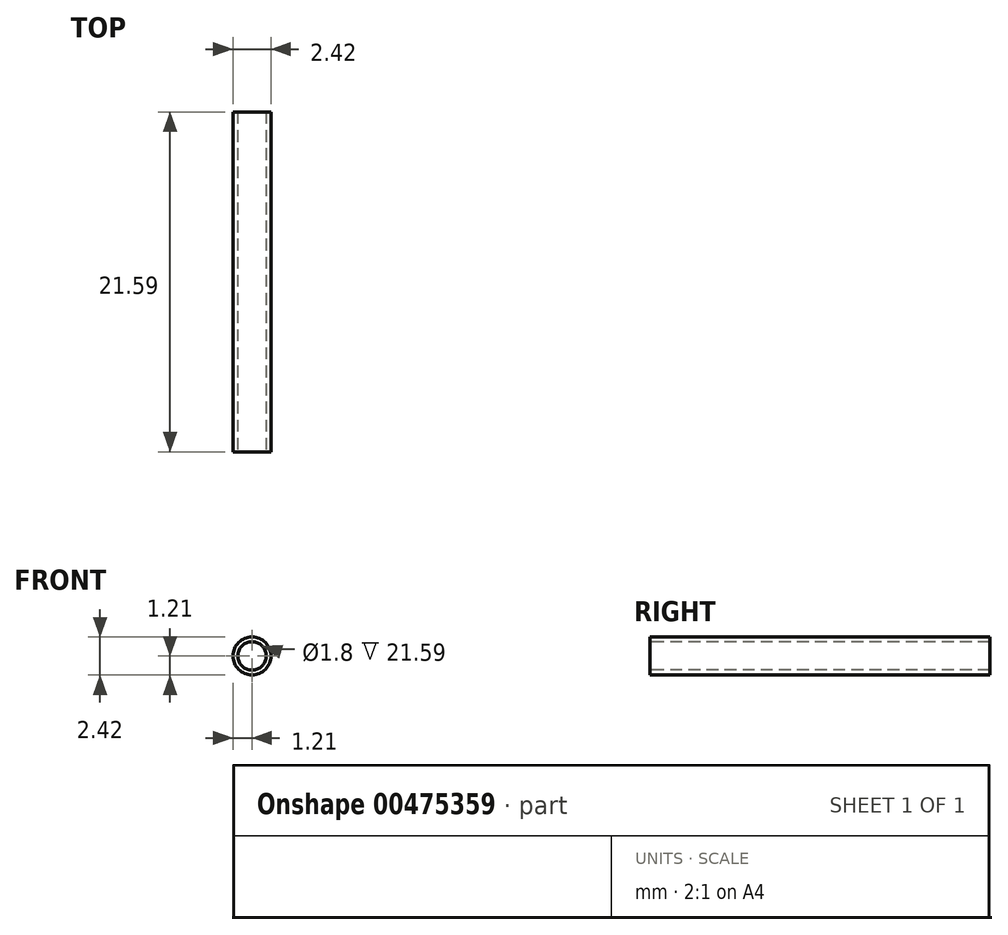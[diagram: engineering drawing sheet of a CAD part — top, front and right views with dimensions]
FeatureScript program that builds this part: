
annotation { "Feature Type Name" : "Feature", "Feature Type Description" : "" }
export const myFeature = defineFeature(function(context is Context, id is Id, definition is map)
    precondition{}
    {
        {
            var Q0;
            Q0=qCreatedBy(makeId("Right.planeOp"),FACE);
            var sketch = newSketch(context, id + "F0", { "sketchPlane" : qUnion([Q0])});
            skLineSegment(sketch, "E0.bottom", {"start": v(0, 0.9) * mm, "end": v(21.59, 0.9) * mm});
            skLineSegment(sketch, "E0.top", {"start": v(0, 1.2) * mm, "end": v(21.59, 1.2) * mm});
            skLineSegment(sketch, "E0.left", {"start": v(0, 0.9) * mm, "end": v(0, 1.2) * mm});
            skLineSegment(sketch, "E0.right", {"start": v(21.59, 0.9) * mm, "end": v(21.59, 1.2) * mm});
            skLineSegment(sketch, "E1", {"start": v(0, 0) * mm, "end": v(22.47, 0) * mm, "construction": true});
            skSolve(sketch);
        }
        {
            var Q0;
            Q0 = qSketchRegion(id + "F0", true);
            var Q1;
            Q1=sQuery(id+"F0.wireOp",EDGE,"E1");
            revolve(context, id + "F1", {"entities" : qUnion([Q0]), "axis" : qUnion([Q1]), "revolveType" : RevolveType.FULL});
        }
    });
